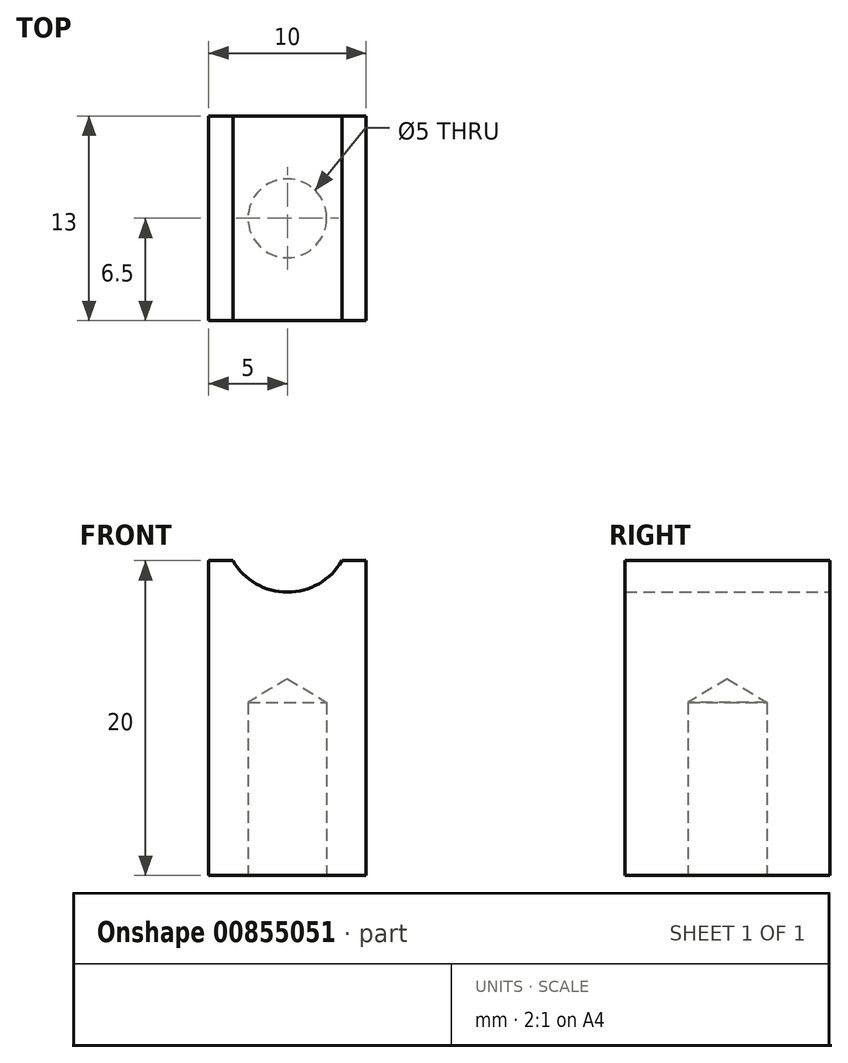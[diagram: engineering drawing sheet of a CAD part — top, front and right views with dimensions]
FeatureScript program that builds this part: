
annotation { "Feature Type Name" : "Feature", "Feature Type Description" : "" }
export const myFeature = defineFeature(function(context is Context, id is Id, definition is map)
    precondition{}
    {
        {
            var Q0;
            Q0=qCreatedBy(makeId("Front.planeOp"),FACE);
            var sketch = newSketch(context, id + "F0", { "sketchPlane" : qUnion([Q0])});
            skLineSegment(sketch, "E0.bottom", {"start": v(0, 0) * mm, "end": v(10, 0) * mm});
            skLineSegment(sketch, "E0.top", {"start": v(0, 20) * mm, "end": v(1.54, 20) * mm});
            skLineSegment(sketch, "E0.left", {"start": v(0, 0) * mm, "end": v(0, 20) * mm});
            skLineSegment(sketch, "E0.right", {"start": v(10, 0) * mm, "end": v(10, 20) * mm});
            skArc(sketch, "E1", {"start": v(1.54, 20) * mm, "mid": v(5, 18) * mm, "end": v(8.46, 20) * mm});
            skLineSegment(sketch, "E2", {"start": v(5, 20) * mm, "end": v(5, 0) * mm, "construction": true});
            skLineSegment(sketch, "E3.trimOffspring", {"start": v(8.46, 20) * mm, "end": v(10, 20) * mm});
            skSolve(sketch);
        }
        {
            var Q0;
            Q0 = qSketchRegion(id + "F0", true);
            extrude(context, id + "F1", {"entities" : qUnion([Q0]), "depth" : 13 * mm, "offsetDistance" : 25 * mm, "symmetric" : true});
        }
        {
            var Q0;
            Q0=makeQuery(id+"F1.opExtrude","SWEPT_FACE",FACE,{"disambiguationData":[OSD([sQuery(id+"F0.wireOp",EDGE,"E0.bottom")])]});
            var sketch = newSketch(context, id + "F2", { "sketchPlane" : qUnion([Q0])});
            skLineSegment(sketch, "E4", {"start": v(10, -6.5) * mm, "end": v(0, 6.5) * mm, "construction": true});
            skLineSegment(sketch, "E5", {"start": v(10, 6.5) * mm, "end": v(0, -6.5) * mm, "construction": true});
            skPoint(sketch, "E6", {"position": v(5, 0) * mm});
            skSolve(sketch);
        }
        {
            var Q0;
            Q0=sQuery(id+"F2.wireOp",VERTEX,"E6");
            var Q1;
            Q1=makeQuery(id+"F1.opExtrude","SWEPT_BODY",BODY,{"disambiguationData":[OSD([sQuery(id+"F0.wireOp",EDGE,"E0.bottom"),sQuery(id+"F0.wireOp",EDGE,"E0.top"),sQuery(id+"F0.wireOp",EDGE,"E0.left"),sQuery(id+"F0.wireOp",EDGE,"E0.right"),sQuery(id+"F0.wireOp",EDGE,"E1"),sQuery(id+"F0.wireOp",EDGE,"E3.trimOffspring")])]});
            hole(context, id + "F3", {"style" : HoleStyle.SIMPLE, "endStyle" : HoleEndStyle.BLIND, "standardTappedOrClearance" : lookupTablePath({ "standard" : "ISO", "engagement" : "75%", "pitch" : "1 mm", "size" : "M6", "type" : "Tapped" }), "standardBlindInLast" : lookupTablePath({ "standard" : "ISO", "fit" : "Normal", "engagement" : "75%", "pitch" : "1 mm", "size" : "M6", "type" : "Clearance & tapped" }), "holeDiameter" : 5 * mm, "majorDiameter" : 6 * mm, "showTappedDepth" : true, "holeDepth" : 11 * mm, "isTappedThrough" : true, "tappedDepth" : 8 * mm, "tapClearance" : 3, "startFromSketch" : true, "locations" : qUnion([Q0]), "scope" : qUnion([Q1])});
        }
    });
